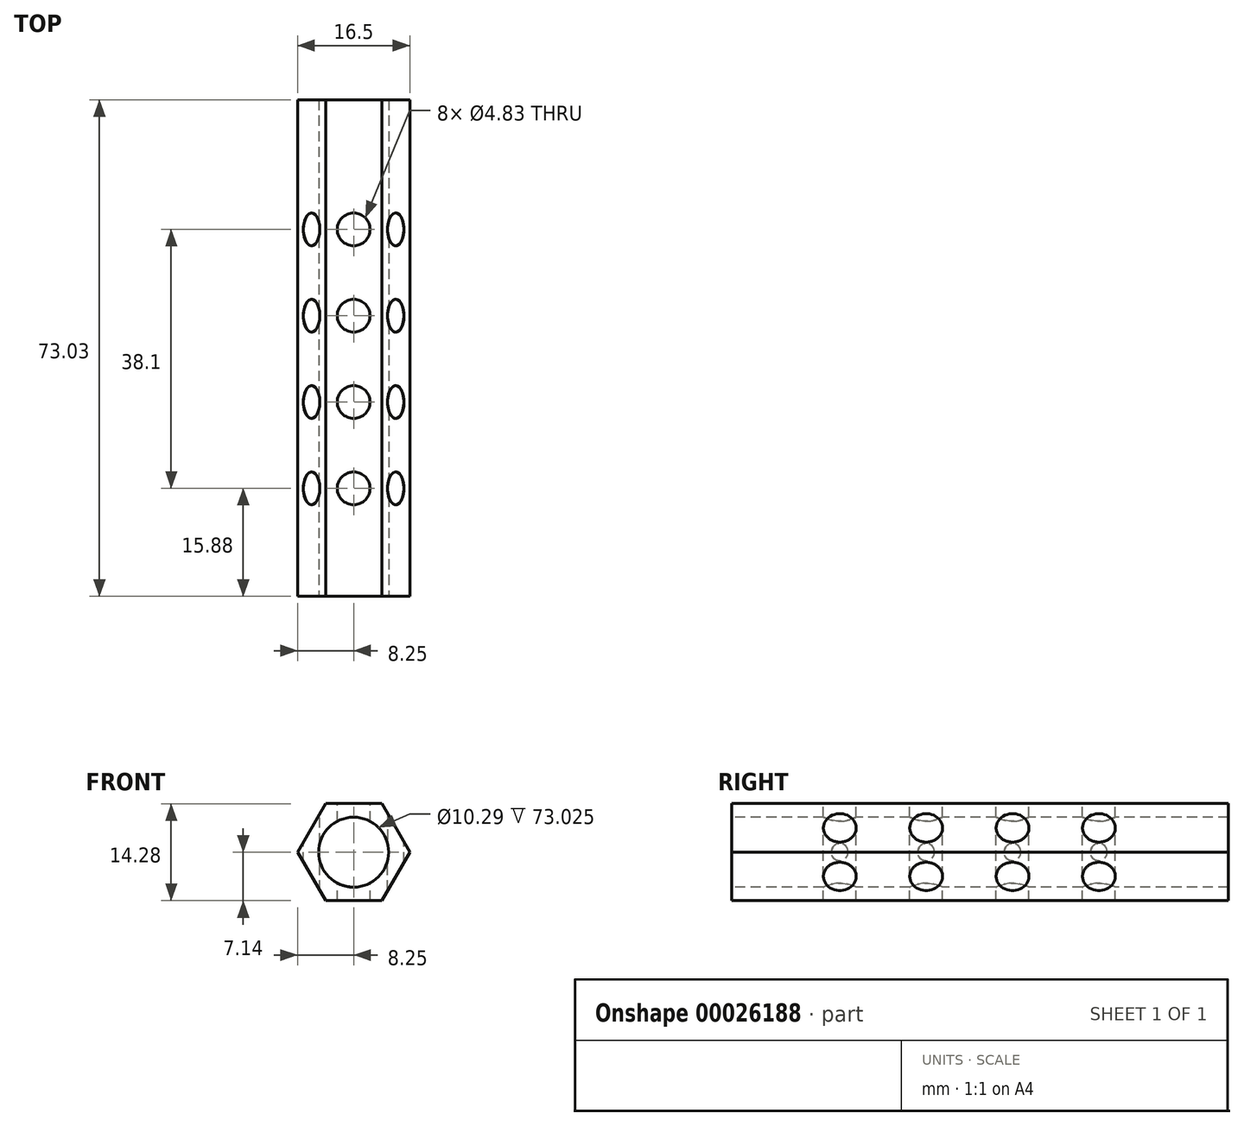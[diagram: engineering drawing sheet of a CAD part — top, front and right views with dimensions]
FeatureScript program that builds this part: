
annotation { "Feature Type Name" : "Feature", "Feature Type Description" : "" }
export const myFeature = defineFeature(function(context is Context, id is Id, definition is map)
    precondition{}
    {
        {
            var Q0;
            Q0=qCreatedBy(makeId("Front.planeOp"),FACE);
            var sketch = newSketch(context, id + "F0", { "sketchPlane" : qUnion([Q0])});
            skCircle(sketch, "E0.cCircle", {"center": v(0, 0) * mm, "radius": 7.14 * mm, "construction": true});
            skLineSegment(sketch, "E0.0", {"start": v(4.12, -7.14) * mm, "end": v(-4.12, -7.14) * mm});
            skLineSegment(sketch, "E0.1", {"start": v(-4.12, -7.14) * mm, "end": v(-8.25, 0) * mm});
            skLineSegment(sketch, "E0.2", {"start": v(-8.25, 0) * mm, "end": v(-4.12, 7.14) * mm});
            skLineSegment(sketch, "E0.3", {"start": v(-4.12, 7.14) * mm, "end": v(4.12, 7.14) * mm});
            skLineSegment(sketch, "E0.4", {"start": v(4.12, 7.14) * mm, "end": v(8.25, 0) * mm});
            skLineSegment(sketch, "E0.5", {"start": v(8.25, 0) * mm, "end": v(4.12, -7.14) * mm});
            skPoint(sketch, "E0.0.midPoint", {"position": v(0, -7.14) * mm});
            skSolve(sketch);
        }
        {
            var Q0;
            Q0=makeQuery(id+"F0.imprint","IMPRINT",FACE,{"disambiguationData":[TD([[makeQuery(id+"F0.imprint","IMPRINT",EDGE,{"derivedFrom":sQuery(id+"F0.wireOp",EDGE,"E0.0")}),-1.0]])]});
            extrude(context, id + "F1", {"entities" : qUnion([Q0]), "depth" : 73.02 * mm});
        }
        {
            var Q0;
            Q0=makeQuery(id+"F1.opExtrude","CAP_FACE",FACE,{"disambiguationData":[OSD([sQuery(id+"F0.wireOp",EDGE,"E0.0"),sQuery(id+"F0.wireOp",EDGE,"E0.1"),sQuery(id+"F0.wireOp",EDGE,"E0.2"),sQuery(id+"F0.wireOp",EDGE,"E0.3"),sQuery(id+"F0.wireOp",EDGE,"E0.4"),sQuery(id+"F0.wireOp",EDGE,"E0.5")])],"isStart":false});
            var sketch = newSketch(context, id + "F2", { "sketchPlane" : qUnion([Q0])});
            skCircle(sketch, "E1", {"center": v(0, 0) * mm, "radius": 5.14 * mm});
            skSolve(sketch);
        }
        {
            var Q0;
            Q0=makeQuery(id+"F2.imprint","IMPRINT",FACE,{"disambiguationData":[TD([[makeQuery(id+"F2.imprint","IMPRINT",EDGE,{"derivedFrom":sQuery(id+"F2.wireOp",EDGE,"E1")}),1.0]])]});
            extrude(context, id + "F3", {"entities" : qUnion([Q0]), "operationType" : NewBodyOperationType.REMOVE, "endBound" : BoundingType.THROUGH_ALL, "oppositeDirection" : true, "depth" : 25.4 * mm});
        }
        {
            var Q0;
            Q0=makeQuery(id+"F1.opExtrude","SWEPT_FACE",FACE,{"disambiguationData":[OSD([sQuery(id+"F0.wireOp",EDGE,"E0.4")])]});
            var sketch = newSketch(context, id + "F4", { "sketchPlane" : qUnion([Q0])});
            skLineSegment(sketch, "E2", {"start": v(-73.03, 0) * mm, "end": v(0, 0) * mm, "construction": true});
            skCircle(sketch, "E3", {"center": v(-57.15, 0) * mm, "radius": 2.41 * mm});
            skCircle(sketch, "E4", {"center": v(-44.45, 0) * mm, "radius": 2.41 * mm});
            skCircle(sketch, "E5", {"center": v(-31.75, 0) * mm, "radius": 2.41 * mm});
            skCircle(sketch, "E6", {"center": v(-19.05, 0) * mm, "radius": 2.41 * mm});
            skSolve(sketch);
        }
        {
            var Q0;
            Q0=makeQuery(id+"F1.opExtrude","SWEPT_FACE",FACE,{"disambiguationData":[OSD([sQuery(id+"F0.wireOp",EDGE,"E0.3")])]});
            var sketch = newSketch(context, id + "F5", { "sketchPlane" : qUnion([Q0])});
            skPoint(sketch, "E7", {"position": v(0, -73.03) * mm});
            skLineSegment(sketch, "E8", {"start": v(0, 0) * mm, "end": v(0, -73.03) * mm, "construction": true});
            skCircle(sketch, "E9", {"center": v(0, -19.05) * mm, "radius": 2.41 * mm});
            skCircle(sketch, "E10", {"center": v(0, -31.75) * mm, "radius": 2.41 * mm});
            skCircle(sketch, "E11", {"center": v(0, -44.45) * mm, "radius": 2.41 * mm});
            skCircle(sketch, "E12", {"center": v(0, -57.15) * mm, "radius": 2.41 * mm});
            skSolve(sketch);
        }
        {
            var Q0;
            Q0=makeQuery(id+"F1.opExtrude","SWEPT_FACE",FACE,{"disambiguationData":[OSD([sQuery(id+"F0.wireOp",EDGE,"E0.2")])]});
            var sketch = newSketch(context, id + "F6", { "sketchPlane" : qUnion([Q0])});
            skCircle(sketch, "E13", {"center": v(31.75, 0) * mm, "radius": 2.41 * mm});
            skCircle(sketch, "E14", {"center": v(44.45, 0) * mm, "radius": 2.41 * mm});
            skCircle(sketch, "E15", {"center": v(19.05, 0) * mm, "radius": 2.41 * mm});
            skCircle(sketch, "E16", {"center": v(57.15, 0) * mm, "radius": 2.41 * mm});
            skLineSegment(sketch, "E17", {"start": v(0, 0) * mm, "end": v(73.03, 0) * mm, "construction": true});
            skSolve(sketch);
        }
        {
            var Q0;
            Q0=makeQuery(id+"F5.imprint","IMPRINT",FACE,{"disambiguationData":[TD([[makeQuery(id+"F5.imprint","IMPRINT",EDGE,{"derivedFrom":sQuery(id+"F5.wireOp",EDGE,"E9")}),1.0]])]});
            var Q1;
            Q1=makeQuery(id+"F4.imprint","IMPRINT",FACE,{"disambiguationData":[TD([[makeQuery(id+"F4.imprint","IMPRINT",EDGE,{"derivedFrom":sQuery(id+"F4.wireOp",EDGE,"E6")}),1.0]])]});
            var Q2;
            Q2=makeQuery(id+"F4.imprint","IMPRINT",FACE,{"disambiguationData":[TD([[makeQuery(id+"F4.imprint","IMPRINT",EDGE,{"derivedFrom":sQuery(id+"F4.wireOp",EDGE,"E5")}),1.0]])]});
            var Q3;
            Q3=makeQuery(id+"F5.imprint","IMPRINT",FACE,{"disambiguationData":[TD([[makeQuery(id+"F5.imprint","IMPRINT",EDGE,{"derivedFrom":sQuery(id+"F5.wireOp",EDGE,"E10")}),1.0]])]});
            var Q4;
            Q4=makeQuery(id+"F5.imprint","IMPRINT",FACE,{"disambiguationData":[TD([[makeQuery(id+"F5.imprint","IMPRINT",EDGE,{"derivedFrom":sQuery(id+"F5.wireOp",EDGE,"E11")}),1.0]])]});
            var Q5;
            Q5=makeQuery(id+"F4.imprint","IMPRINT",FACE,{"disambiguationData":[TD([[makeQuery(id+"F4.imprint","IMPRINT",EDGE,{"derivedFrom":sQuery(id+"F4.wireOp",EDGE,"E4")}),1.0]])]});
            var Q6;
            Q6=makeQuery(id+"F4.imprint","IMPRINT",FACE,{"disambiguationData":[TD([[makeQuery(id+"F4.imprint","IMPRINT",EDGE,{"derivedFrom":sQuery(id+"F4.wireOp",EDGE,"E3")}),1.0]])]});
            var Q7;
            Q7=makeQuery(id+"F5.imprint","IMPRINT",FACE,{"disambiguationData":[TD([[makeQuery(id+"F5.imprint","IMPRINT",EDGE,{"derivedFrom":sQuery(id+"F5.wireOp",EDGE,"E12")}),1.0]])]});
            var Q8;
            Q8=makeQuery(id+"F6.imprint","IMPRINT",FACE,{"disambiguationData":[TD([[makeQuery(id+"F6.imprint","IMPRINT",EDGE,{"derivedFrom":sQuery(id+"F6.wireOp",EDGE,"E15")}),1.0]])]});
            var Q9;
            Q9=makeQuery(id+"F6.imprint","IMPRINT",FACE,{"disambiguationData":[TD([[makeQuery(id+"F6.imprint","IMPRINT",EDGE,{"derivedFrom":sQuery(id+"F6.wireOp",EDGE,"E13")}),1.0]])]});
            var Q10;
            Q10=makeQuery(id+"F6.imprint","IMPRINT",FACE,{"disambiguationData":[TD([[makeQuery(id+"F6.imprint","IMPRINT",EDGE,{"derivedFrom":sQuery(id+"F6.wireOp",EDGE,"E14")}),1.0]])]});
            var Q11;
            Q11=makeQuery(id+"F6.imprint","IMPRINT",FACE,{"disambiguationData":[TD([[makeQuery(id+"F6.imprint","IMPRINT",EDGE,{"derivedFrom":sQuery(id+"F6.wireOp",EDGE,"E16")}),1.0]])]});
            extrude(context, id + "F7", {"entities" : qUnion([Q0, Q1, Q2, Q3, Q4, Q5, Q6, Q7, Q8, Q9, Q10, Q11]), "operationType" : NewBodyOperationType.REMOVE, "endBound" : BoundingType.THROUGH_ALL, "oppositeDirection" : true, "depth" : 25.4 * mm});
        }
    });
